# Revit family: LUXI_HIGH BAY LIGHT_DM
name_source: partatom
category: Apparecchi per illuminazione
revit_build: Autodesk Revit 2016 (Build: 20161004_0715(x64)
units: mm (PartAtom-declared; Revit-internal decimal feet)

## family parameters
Condiviso = No
Host = Superficie
Numero OmniClass = 23.80.70.00
Punto di calcolo locali = Sì
Quota connettore circolare = Usa diametro
Sorgente d'illuminazione = Sì
Taglio con vuoti quando caricato = No
Tipo di parte = Normale
Titolo OmniClass = Lighting

## types (2) — shared parameters
Alimentatore = Incluso
Alimentazione = 220-240V AC / 50-60 Hz
Angolo inclinazione = -90.00°
Certificazioni = CE / RohS
Classe di efficienza energetica = A++
Classe di protezione = I
Classe di rischio fotobiologico = Esente (RG0)
Colore = Nero
Descrizione = Proiettore a LED
Fattore di correzione di potenza = ≥0,95 (typ.)
Filtro dei colori = 16777215
Garanzia = 5 anni
Grado di protezione = IP 65
IFCExportAs = IfcLightFixtureType
Indice di resa cromatica = ≥80 (typ.)
Masterformat 2016 Codice = 26.50.00
Masterformat 2016 Descrizione = Lighting
Materiale 1 = Alluminio_Nero
Materiale 2 = Polietilentereflato anti-ingiallimento
Modello = Serie DM| High Bay Light
OFF6 = 5 mm  [stored 0.0164042 ft]
Ottiche = Lenti
Produttore = Luxi Illuminazione S.r.l.
Prospetto di default = 2000 mm  [stored 6.56168 ft]
Protezione agli urti = IK10 (20 Joule)
Regolazione del flusso luminoso = 1-10V
Rendi la forma visibile nel rendering = No
Revisione = 3
Sistema di illuminazione = Luce diretta downlight
Sorgente = LED SMD
Step MacAdam (SDCM) = <4
Temperatura di esercizio = -30°C / +45°C
Tipologie di installazione = Sospensione / parete / soffitto
URL = https://www.luxi.lighting
Uniclass 2015 Codice = EF_70_80
Uniclass 2015 Descrizione = Lighting
Variazione temperatura colore lampada con luminosità attenuata = <Nessuno>
Vita utile = L70B20 50.000ore

## per-type parameters (varying)
| type | Carico apparente | Diametro | Dimensioni | Emetti da diametro cerchio | File diagramma fotometrico | H | Lunghezza | OFF1 | OFF2 | OFF3 | OFF4 | OFF5 | Peso | Potenza | Raggio Int. |
| HBDM100095B840D | 100 VA | 270 mm  [stored 0.885827 ft] | Ø270x160 | 224 mm | HBDM100095B840D Luxi SERIE DM 100W 4000K 90°.IES | 160 mm  [stored 0.524934 ft] | 135 mm  [stored 0.442913 ft] | 3 mm  [stored 0.00984252 ft] | 9 mm  [stored 0.0295276 ft] | 13 mm | 90 mm  [stored 0.295276 ft] | 10 mm  [stored 0.0328084 ft] | 2.60 kg | 100 W | 16 mm  [stored 0.0524934 ft] |
| HBDM150090B840D | 150 VA | 340 mm  [stored 1.11549 ft] | Ø340x170 | 294 mm | HBDM150090B840D Luxi SERIE DM 150W 4000K 90°.IES | 170 mm  [stored 0.557743 ft] | 170 mm  [stored 0.557743 ft] | 8 mm  [stored 0.0262467 ft] | 6 mm  [stored 0.019685 ft] | 15 mm | 125 mm | 11 mm | 3.50 kg | 150 W | 20 mm |

note: column(s) folded — value = type name in every type: Articolo

note: [stored X ft] marks values corroborated as IEEE doubles in the binary element streams (Revit-internal decimal feet)
